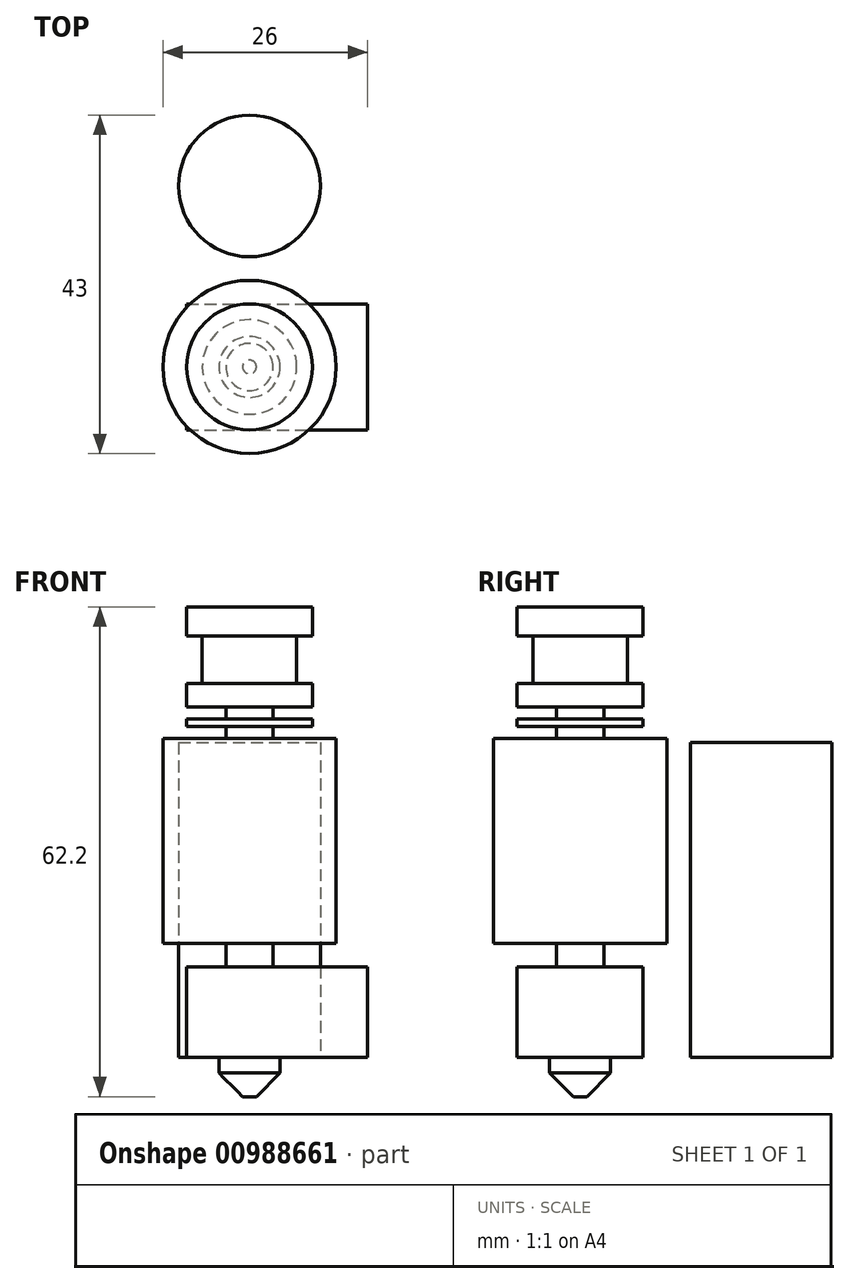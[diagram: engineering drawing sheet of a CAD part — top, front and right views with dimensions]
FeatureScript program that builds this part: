
annotation { "Feature Type Name" : "Feature", "Feature Type Description" : "" }
export const myFeature = defineFeature(function(context is Context, id is Id, definition is map)
    precondition{}
    {
        {
            var Q0;
            Q0=qCreatedBy(makeId("Front.planeOp"),FACE);
            var sketch = newSketch(context, id + "F0", { "sketchPlane" : qUnion([Q0])});
            skLineSegment(sketch, "E0", {"start": v(0, 42.7) * mm, "end": v(-8, 42.7) * mm});
            skLineSegment(sketch, "E1", {"start": v(-8, 42.7) * mm, "end": v(-8, 39) * mm});
            skLineSegment(sketch, "E2", {"start": v(-8, 39) * mm, "end": v(-6, 39) * mm});
            skLineSegment(sketch, "E3", {"start": v(-6, 39) * mm, "end": v(-6, 33) * mm});
            skLineSegment(sketch, "E4", {"start": v(-6, 33) * mm, "end": v(-8, 33) * mm});
            skLineSegment(sketch, "E5", {"start": v(-8, 33) * mm, "end": v(-8, 30) * mm});
            skLineSegment(sketch, "E6", {"start": v(-8, 30) * mm, "end": v(-3, 30) * mm});
            skLineSegment(sketch, "E7", {"start": v(-3, 26) * mm, "end": v(-11, 26) * mm});
            skLineSegment(sketch, "E8", {"start": v(-11, 26) * mm, "end": v(-11, 0) * mm});
            skLineSegment(sketch, "E9", {"start": v(0, 42.7) * mm, "end": v(0, 0) * mm});
            skLineSegment(sketch, "E10", {"start": v(-8, 28.5) * mm, "end": v(-8, 27.5) * mm});
            skLineSegment(sketch, "E11", {"start": v(-8, 27.5) * mm, "end": v(-3, 27.5) * mm});
            skLineSegment(sketch, "E12", {"start": v(-3, 27.5) * mm, "end": v(-3, 26) * mm});
            skLineSegment(sketch, "E13", {"start": v(-8, 28.5) * mm, "end": v(-3, 28.5) * mm});
            skLineSegment(sketch, "E14", {"start": v(-3, 28.5) * mm, "end": v(-3, 30) * mm});
            skLineSegment(sketch, "E15", {"start": v(-11, 0) * mm, "end": v(-3, 0) * mm});
            skLineSegment(sketch, "E16", {"start": v(-3, 0) * mm, "end": v(-3, -3) * mm});
            skLineSegment(sketch, "E17", {"start": v(-3, -3) * mm, "end": v(0, -3) * mm});
            skLineSegment(sketch, "E18", {"start": v(0, -3) * mm, "end": v(0, 0) * mm});
            skSolve(sketch);
        }
        {
            var Q0;
            Q0 = qSketchRegion(id + "F0", true);
            var Q1;
            Q1=sQuery(id+"F0.wireOp",EDGE,"E9");
            revolve(context, id + "F1", {"surfaceOperationType" : NewSurfaceOperationType.NEW, "entities" : qUnion([Q0]), "axis" : qUnion([Q1]), "revolveType" : RevolveType.FULL});
        }
        {
            var Q0;
            Q0=makeQuery(id+"F1.opRevolve","SWEPT_FACE",FACE,{"disambiguationData":[OSD([sQuery(id+"F0.wireOp",EDGE,"E17")])]});
            var sketch = newSketch(context, id + "F2", { "sketchPlane" : qUnion([Q0])});
            skLineSegment(sketch, "E19.bottom", {"start": v(-8, 8) * mm, "end": v(15, 8) * mm});
            skLineSegment(sketch, "E19.top", {"start": v(-8, -8) * mm, "end": v(15, -8) * mm});
            skLineSegment(sketch, "E19.left", {"start": v(-8, 8) * mm, "end": v(-8, -8) * mm});
            skLineSegment(sketch, "E19.right", {"start": v(15, 8) * mm, "end": v(15, -8) * mm});
            skSolve(sketch);
        }
        {
            var Q0;
            Q0 = qSketchRegion(id + "F2", true);
            extrude(context, id + "F3", {"entities" : qUnion([Q0]), "operationType" : NewBodyOperationType.ADD, "depth" : 11.5 * mm, "offsetDistance" : 25 * mm});
        }
        {
            var Q0;
            Q0=makeQuery(id+"F3.opExtrude","CAP_FACE",FACE,{"disambiguationData":[OSD([sQuery(id+"F2.wireOp",EDGE,"E19.bottom"),sQuery(id+"F2.wireOp",EDGE,"E19.top"),sQuery(id+"F2.wireOp",EDGE,"E19.left"),sQuery(id+"F2.wireOp",EDGE,"E19.right")])],"isStart":false});
            var sketch = newSketch(context, id + "F4", { "sketchPlane" : qUnion([Q0])});
            skCircle(sketch, "E20", {"center": v(0, 0) * mm, "radius": 3.87 * mm});
            skSolve(sketch);
        }
        {
            var Q0;
            Q0=makeQuery(id+"F4.imprint","IMPRINT",FACE,{"disambiguationData":[TD([[makeQuery(id+"F4.imprint","IMPRINT",EDGE,{"derivedFrom":sQuery(id+"F4.wireOp",EDGE,"E20")}),1.0]])]});
            extrude(context, id + "F5", {"entities" : qUnion([Q0]), "operationType" : NewBodyOperationType.ADD, "depth" : 2 * mm, "offsetDistance" : 25 * mm, "hasSecondDirectionDraft" : true, "secondDirectionDraftAngle" : 45 * degree, "secondDirectionDraftPullDirection" : true});
        }
        {
            var Q0;
            Q0=makeQuery(id+"F5.opExtrude","CAP_FACE",FACE,{"disambiguationData":[OSD([sQuery(id+"F4.wireOp",EDGE,"E20")])],"isStart":false});
            extrude(context, id + "F6", {"entities" : qUnion([Q0]), "operationType" : NewBodyOperationType.ADD, "depth" : 3 * mm, "offsetDistance" : 25 * mm, "hasDraft" : true, "draftAngle" : 45 * degree, "draftPullDirection" : true});
        }
        {
            var Q0;
            Q0=makeQuery(id+"F3.opExtrude","CAP_FACE",FACE,{"disambiguationData":[OSD([sQuery(id+"F2.wireOp",EDGE,"E19.bottom"),sQuery(id+"F2.wireOp",EDGE,"E19.top"),sQuery(id+"F2.wireOp",EDGE,"E19.left"),sQuery(id+"F2.wireOp",EDGE,"E19.right")])],"isStart":false});
            var sketch = newSketch(context, id + "F7", { "sketchPlane" : qUnion([Q0])});
            skCircle(sketch, "E21", {"center": v(0, -23) * mm, "radius": 9 * mm});
            skSolve(sketch);
        }
        {
            var Q0;
            Q0=makeQuery(id+"F7.imprint","IMPRINT",FACE,{"disambiguationData":[TD([[makeQuery(id+"F7.imprint","IMPRINT",EDGE,{"derivedFrom":sQuery(id+"F7.wireOp",EDGE,"E21")}),1.0]])]});
            extrude(context, id + "F8", {"entities" : qUnion([Q0]), "oppositeDirection" : true, "depth" : 40 * mm, "offsetDistance" : 25 * mm});
        }
    });
